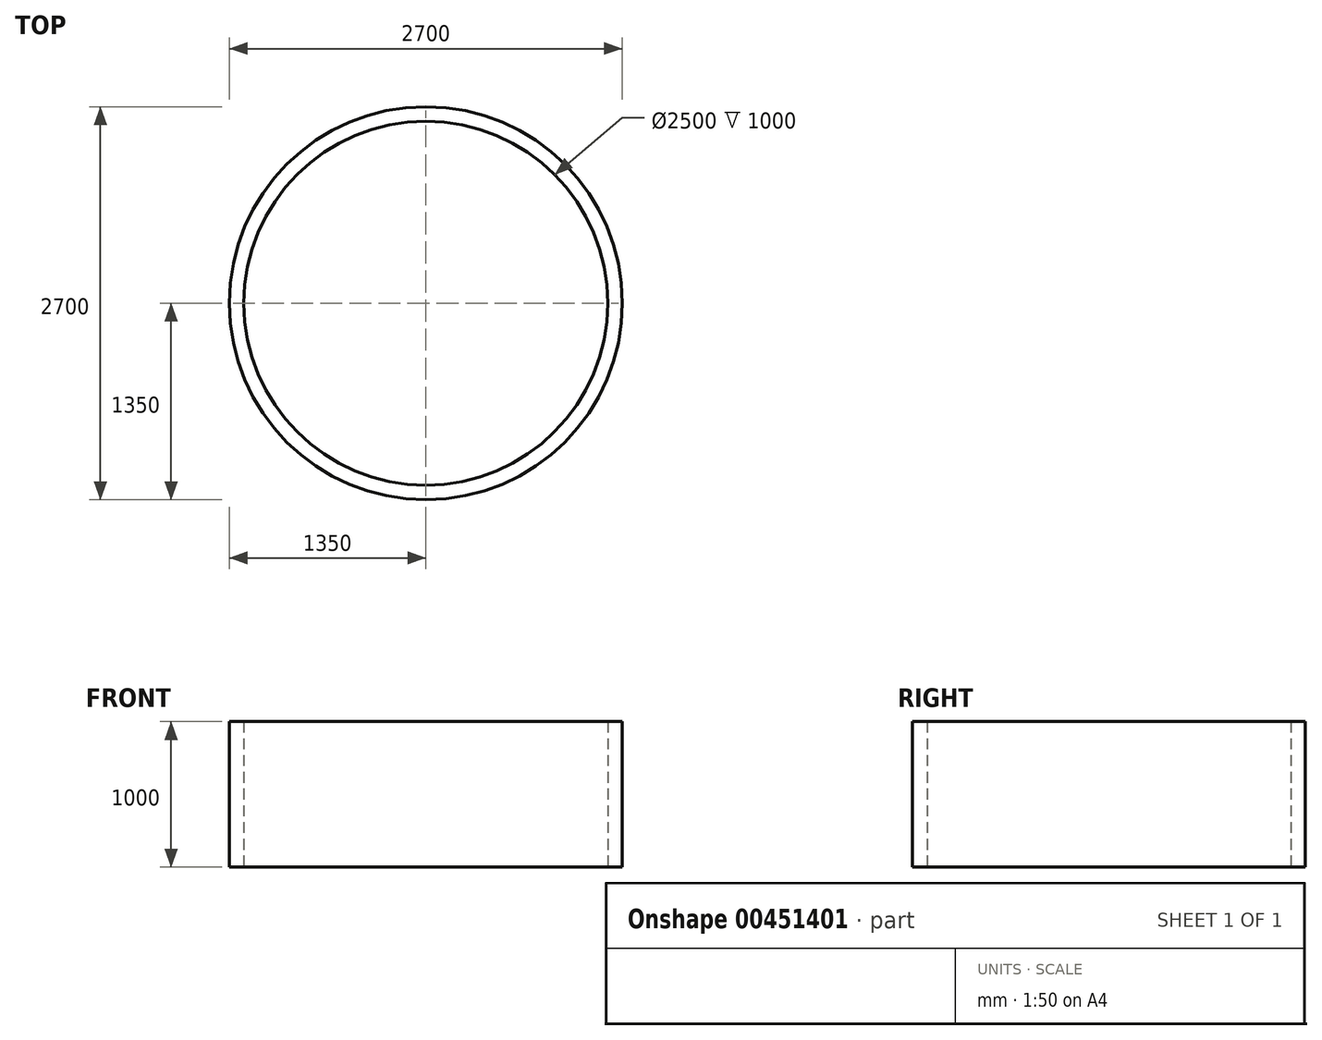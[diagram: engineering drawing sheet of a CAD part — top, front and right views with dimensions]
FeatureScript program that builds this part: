
annotation { "Feature Type Name" : "Feature", "Feature Type Description" : "" }
export const myFeature = defineFeature(function(context is Context, id is Id, definition is map)
    precondition{}
    {
        {
            var Q0;
            Q0=qCreatedBy(makeId("Top.planeOp"),FACE);
            var sketch = newSketch(context, id + "F0", { "sketchPlane" : qUnion([Q0])});
            skCircle(sketch, "E0", {"center": v(0, 0) * mm, "radius": 1350 * mm});
            skCircle(sketch, "E1", {"center": v(0, 0) * mm, "radius": 1250 * mm});
            skSolve(sketch);
        }
        {
            var Q0;
            Q0=makeQuery(id+"F0.imprint","IMPRINT",FACE,{"disambiguationData":[TD([[makeQuery(id+"F0.imprint","IMPRINT",EDGE,{"derivedFrom":sQuery(id+"F0.wireOp",EDGE,"E0")}),1.0]])]});
            extrude(context, id + "F1", {"entities" : qUnion([Q0]), "endBound" : BoundingType.SYMMETRIC, "depth" : 1000 * mm});
        }
    });
